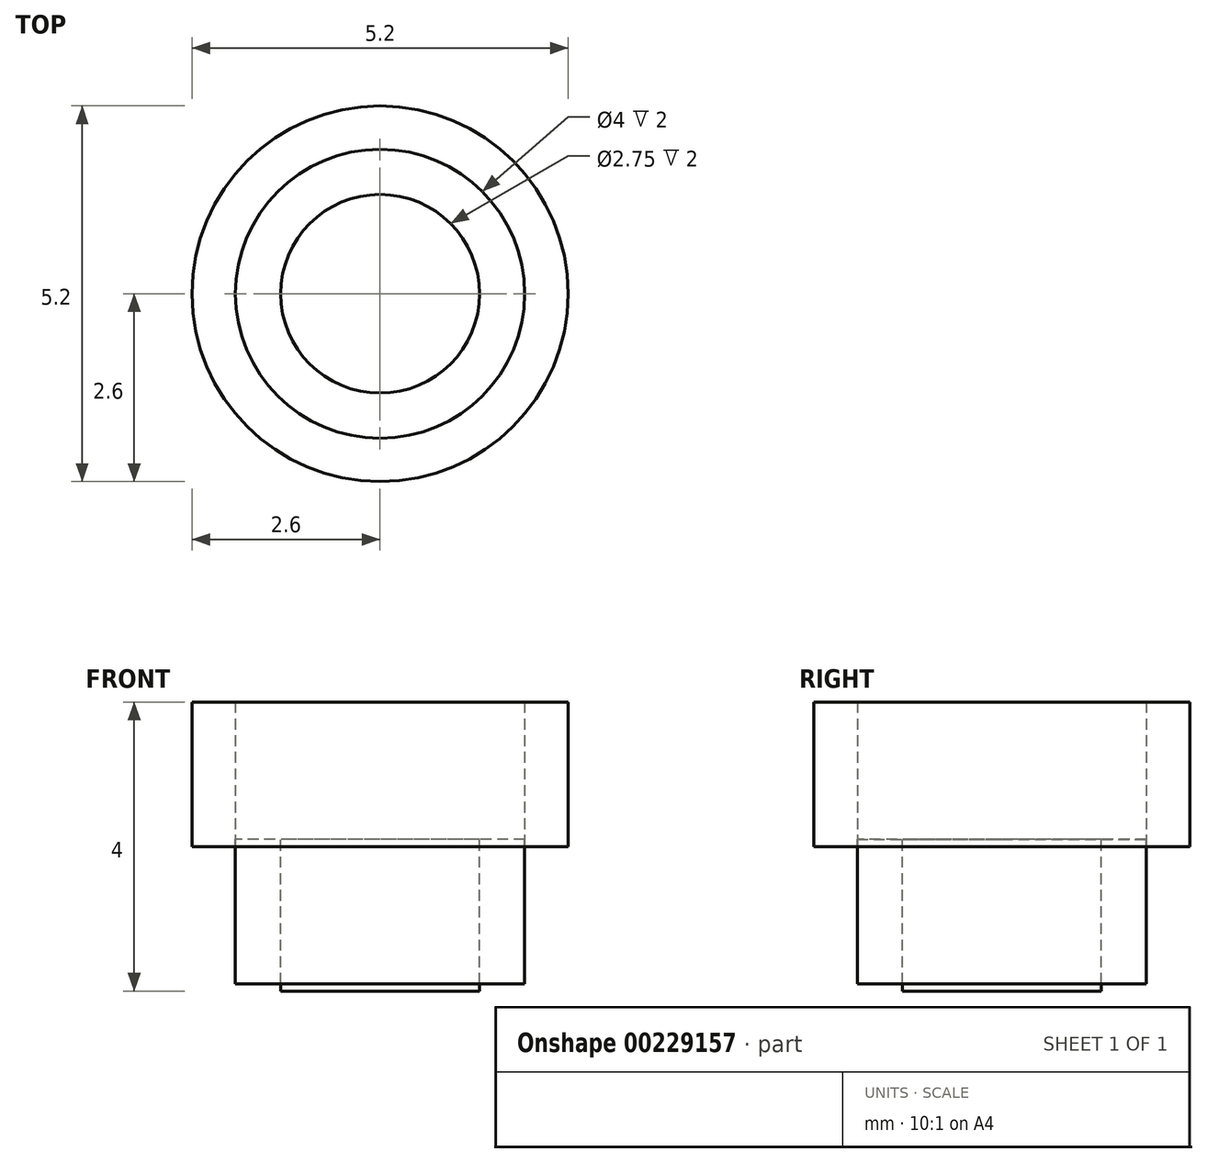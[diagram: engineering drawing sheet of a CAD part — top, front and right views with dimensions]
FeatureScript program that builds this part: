
annotation { "Feature Type Name" : "Feature", "Feature Type Description" : "" }
export const myFeature = defineFeature(function(context is Context, id is Id, definition is map)
    precondition{}
    {
        {
            var Q0;
            Q0=qCreatedBy(makeId("Top.planeOp"),FACE);
            var sketch = newSketch(context, id + "F0", { "sketchPlane" : qUnion([Q0])});
            skCircle(sketch, "E0", {"center": v(0, 0) * mm, "radius": 1.38 * mm});
            skCircle(sketch, "E1", {"center": v(0, 0) * mm, "radius": 2 * mm});
            skSolve(sketch);
        }
        {
            var Q0;
            Q0 = qSketchRegion(id + "F0", true);
            extrude(context, id + "F1", {"entities" : qUnion([Q0]), "oppositeDirection" : true, "depth" : 2 * mm});
        }
        {
            var Q0;
            Q0=makeQuery(id+"F0.imprint","IMPRINT",FACE,{"disambiguationData":[TD([[makeQuery(id+"F0.imprint","IMPRINT",EDGE,{"derivedFrom":sQuery(id+"F0.wireOp",EDGE,"E0")}),1.0]])]});
            extrude(context, id + "F2", {"entities" : qUnion([Q0]), "oppositeDirection" : true, "depth" : 2 * mm});
        }
        {
            var Q0;
            Q0=makeQuery(id+"F0.imprint","IMPRINT",FACE,{"disambiguationData":[TD([[makeQuery(id+"F0.imprint","IMPRINT",EDGE,{"derivedFrom":sQuery(id+"F0.wireOp",EDGE,"E0")}),-1.0]])]});
            var sketch = newSketch(context, id + "F3", { "sketchPlane" : qUnion([Q0])});
            skCircle(sketch, "E2", {"center": v(0, 0) * mm, "radius": 2 * mm});
            skCircle(sketch, "E3", {"center": v(0, 0) * mm, "radius": 2.6 * mm});
            skSolve(sketch);
        }
        {
            var Q0;
            Q0 = qSketchRegion(id + "F3", true);
            extrude(context, id + "F4", {"entities" : qUnion([Q0]), "depth" : 2 * mm});
        }
        {
            var Q0;
            Q0=makeQuery(id+"F1.opExtrude","SWEPT_BODY",BODY,{"disambiguationData":[OSD([sQuery(id+"F0.wireOp",EDGE,"E0"),sQuery(id+"F0.wireOp",EDGE,"E1")])]});
            transform(context, id + "F5", {"entities" : qUnion([Q0]), "transformType" : TransformType.TRANSLATION_3D, "dx" : 0 * mm, "dy" : 0 * mm, "dz" : .1 * mm, "makeCopy" : false});
        }
    });
